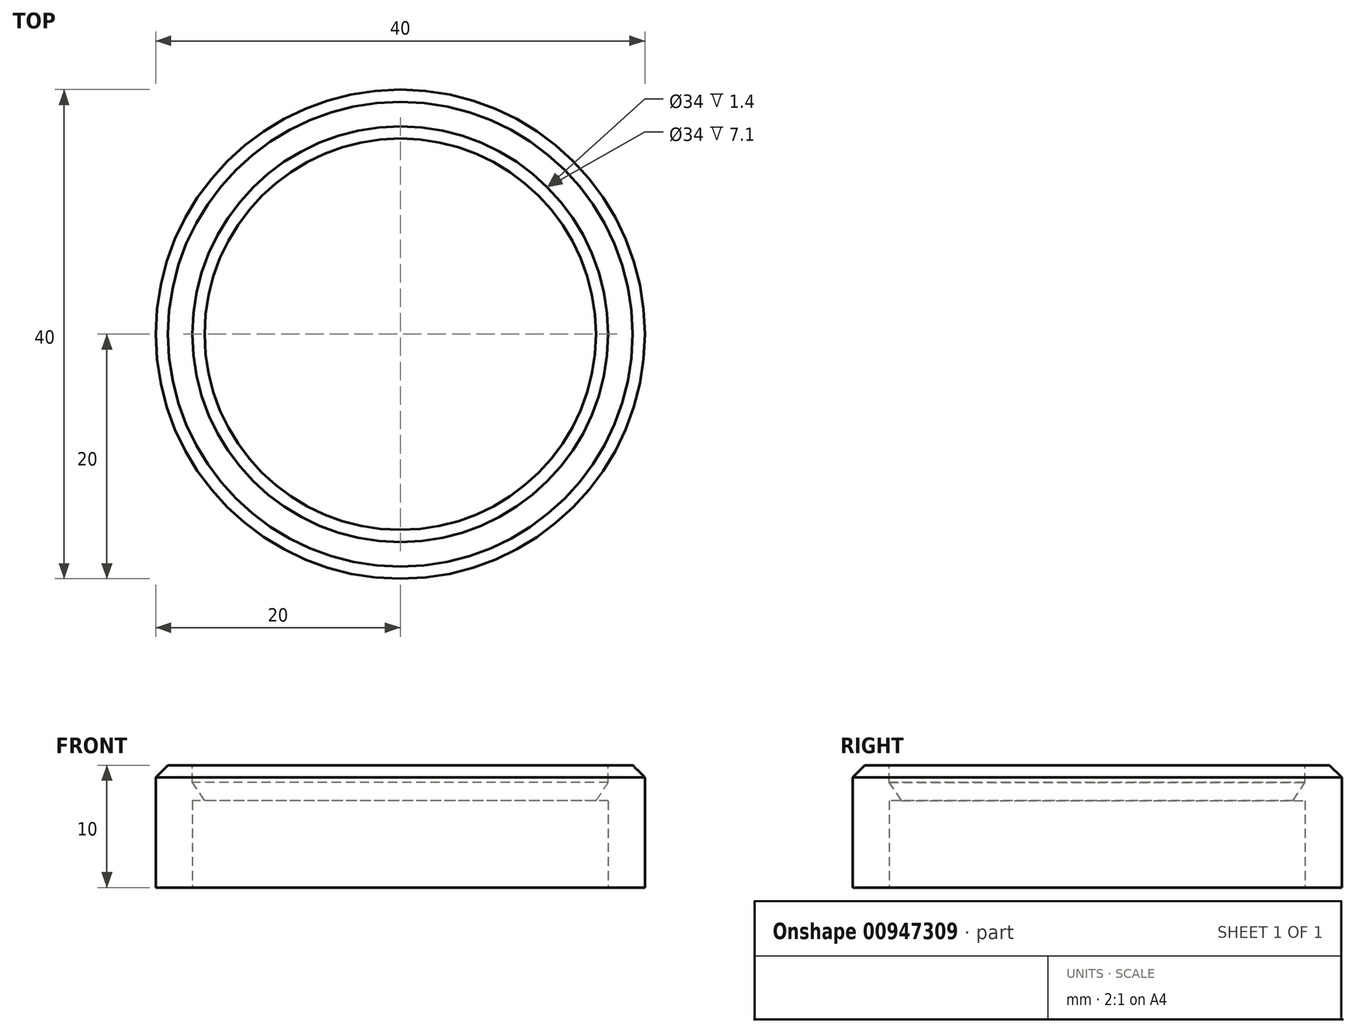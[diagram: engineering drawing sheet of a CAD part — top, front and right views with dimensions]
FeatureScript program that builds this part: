
annotation { "Feature Type Name" : "Feature", "Feature Type Description" : "" }
export const myFeature = defineFeature(function(context is Context, id is Id, definition is map)
    precondition{}
    {
        {
            var Q0;
            Q0=qCreatedBy(makeId("Top.planeOp"),FACE);
            var sketch = newSketch(context, id + "F0", { "sketchPlane" : qUnion([Q0])});
            skCircle(sketch, "E0", {"center": v(0, 0) * mm, "radius": 20 * mm});
            skSolve(sketch);
        }
        {
            var Q0;
            Q0=makeQuery(id+"F0.imprint","IMPRINT",FACE,{"disambiguationData":[TD([[makeQuery(id+"F0.imprint","IMPRINT",EDGE,{"derivedFrom":sQuery(id+"F0.wireOp",EDGE,"E0")}),1.0]])]});
            extrude(context, id + "F1", {"entities" : qUnion([Q0]), "depth" : 10 * mm, "offsetDistance" : 25 * mm});
        }
        {
            var Q0;
            Q0=makeQuery(id+"F1.opExtrude","CAP_FACE",FACE,{"disambiguationData":[OSD([sQuery(id+"F0.wireOp",EDGE,"E0")])],"isStart":false});
            var sketch = newSketch(context, id + "F2", { "sketchPlane" : qUnion([Q0])});
            skCircle(sketch, "E1", {"center": v(0, 0) * mm, "radius": 17 * mm});
            skSolve(sketch);
        }
        {
            var Q0;
            Q0=makeQuery(id+"F2.imprint","IMPRINT",FACE,{"disambiguationData":[TD([[makeQuery(id+"F2.imprint","IMPRINT",EDGE,{"derivedFrom":sQuery(id+"F2.wireOp",EDGE,"E1")}),1.0]])]});
            var Q1;
            Q1=sQuery(id+"F2.wireOp",EDGE,"E1");
            extrude(context, id + "F3", {"entities" : qUnion([Q0]), "operationType" : NewBodyOperationType.REMOVE, "surfaceEntities" : qUnion([Q1]), "oppositeDirection" : true, "depth" : 1.4 * mm, "offsetDistance" : 25 * mm});
        }
        {
            var Q0;
            Q0=makeQuery(id+"F3.boolean.opBoolean","COPY",FACE,{"derivedFrom":makeQuery(id+"F3.opExtrude","CAP_FACE",FACE,{"disambiguationData":[OSD([sQuery(id+"F2.wireOp",EDGE,"E1")])],"isStart":false})});
            cPlane(context, id + "F4", {"entities" : qUnion([Q0]), "cplaneType" : CPlaneType.OFFSET, "offset" : 1.5 * mm, "oppositeDirection" : true, "width" : 150 * mm, "height" : 150 * mm});
        }
        {
            var Q0;
            Q0=qCreatedBy(id+"F4.planeOp",FACE);
            var sketch = newSketch(context, id + "F5", { "sketchPlane" : qUnion([Q0])});
            skCircle(sketch, "E2", {"center": v(0, 0) * mm, "radius": 16 * mm});
            skSolve(sketch);
        }
        {
            var Q1;
            Q1=makeQuery(id+"F3.boolean.opBoolean","COPY",FACE,{"derivedFrom":makeQuery(id+"F3.opExtrude","CAP_FACE",FACE,{"disambiguationData":[OSD([sQuery(id+"F2.wireOp",EDGE,"E1")])],"isStart":false})});
            var Q2;
            Q2 = qSketchRegion(id + "F5", true);
            loft(context, id + "F6", {"operationType" : NewBodyOperationType.REMOVE, "sheetProfilesArray" : [{ "sheetProfileEntities" : qUnion([Q1]) }, { "sheetProfileEntities" : qUnion([Q2]) }]});
        }
        {
            var Q0;
            Q0=makeQuery(id+"F1.opExtrude","CAP_FACE",FACE,{"disambiguationData":[OSD([sQuery(id+"F0.wireOp",EDGE,"E0")])],"isStart":true});
            var sketch = newSketch(context, id + "F7", { "sketchPlane" : qUnion([Q0])});
            skCircle(sketch, "E3", {"center": v(0, 0) * mm, "radius": 17 * mm});
            skSolve(sketch);
        }
        {
            var Q0;
            Q0 = qSketchRegion(id + "F7", true);
            var Q1;
            Q1=makeQuery(id+"F6.boolean.opBoolean","COPY",FACE,{"derivedFrom":makeQuery(id+"F6.opLoft","CAP_FACE",FACE,{"disambiguationData":[OSD([makeQuery(id+"F5.imprint","IMPRINT",FACE,{"disambiguationData":[TD([[makeQuery(id+"F5.imprint","IMPRINT",EDGE,{"derivedFrom":sQuery(id+"F5.wireOp",EDGE,"E2")}),1.0]])]})])],"isStart":true})});
            extrude(context, id + "F8", {"entities" : qUnion([Q0]), "operationType" : NewBodyOperationType.REMOVE, "endBound" : BoundingType.UP_TO_SURFACE, "oppositeDirection" : true, "depth" : 25 * mm, "endBoundEntityFace" : qUnion([Q1]), "offsetDistance" : 25 * mm});
        }
        {
            var Q0;
            Q0=makeQuery(id+"F1.opExtrude","CAP_EDGE",EDGE,{"disambiguationData":[OSD([sQuery(id+"F0.wireOp",EDGE,"E0")])],"isStart":false});
            chamfer(context, id + "F9", {"entities" : qUnion([Q0]), "width" : 1 * mm, "tangentPropagation" : true});
        }
    });
